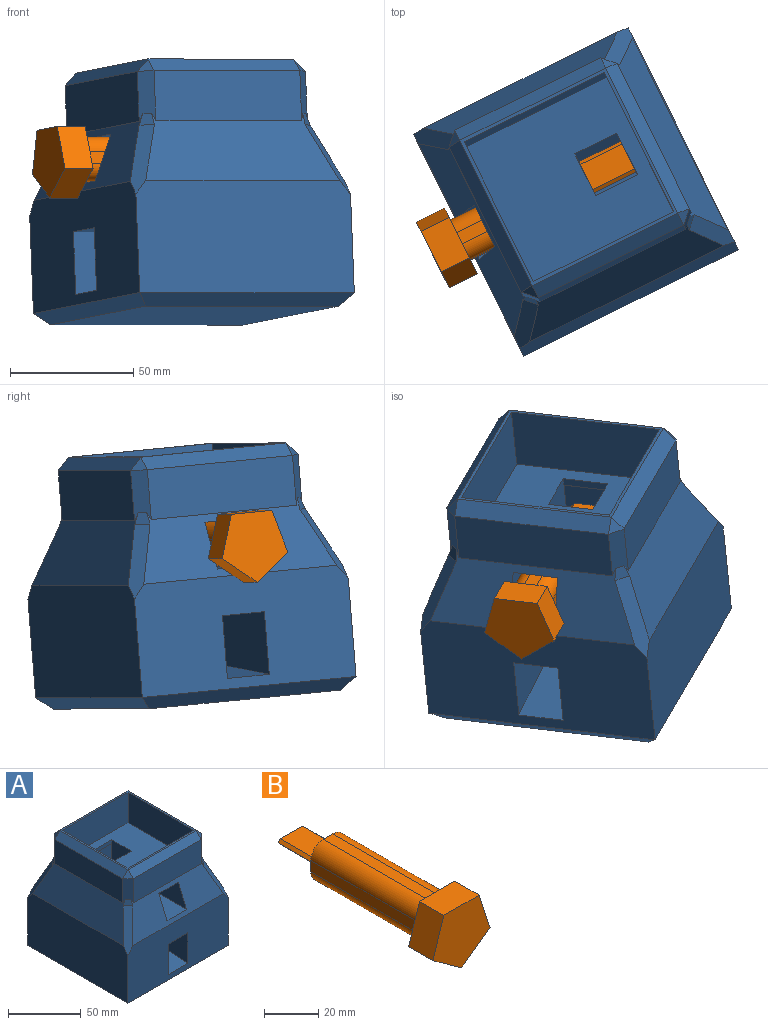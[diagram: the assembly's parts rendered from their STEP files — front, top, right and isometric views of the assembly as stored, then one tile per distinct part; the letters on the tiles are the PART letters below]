
ASSEMBLY  parts=2 mates=1
PART A: 57 faces, bbox 97.2x97.2x101.6 mm
  f0: plane 38.1x19.05mm, normal (0,-1,0), area 725.8mm2, adj f10,f11,f12,f54
  f1: plane 19.05x19.05mm, normal (0,1,0), area 362.9mm2, adj f2,f11,f12,f13
  f2: plane 53.66x19.05mm, normal (0,0,1), area 1022.1mm2, adj f1,f11,f12,f14
  f3: plane 45.77x19.05mm, normal (0,0,-1), area 871.8mm2, adj f4,f11,f12,f14
  f4: plane 19.05x3.18mm, normal (0,1,0), area 60.5mm2, adj f3,f5,f11,f12
  f5: plane 63.5x63.5mm, normal (0,0,1), area 3669.3mm2, adj f4,f6,f11,f12,f20,f21,f22,f27
  f6: plane 19.05x3.18mm, normal (0,-1,0), area 60.5mm2, adj f5,f11,f12,f55
  f7: plane 87.86x28.41mm, normal (0.92,0,0.38), area 2131.3mm2, adj f17,f24,f34,f36,f46,f48,f50,f53
  f8: plane 87.08x27.47mm, normal (0,0.92,0.38), area 2042.9mm2, adj f25,f45,f46,f47,f48,f49,f50,f51
  f9: plane 87.86x28.41mm, normal (-0.92,0,0.38), area 2131.3mm2, adj f15,f26,f33,f35,f45,f47,f51,f52
  f10: plane 74.02x19.05mm, normal (0,-0.09,1), area 1415.5mm2, adj f0,f11,f12,f18
  f11: plane 74.05x66.8mm, normal (1,0,0), area 3383.5mm2, adj f0,f1,f2,f3,f4,f5,f6,f10
  f12: plane 74.05x66.8mm, normal (-1,0,0), area 3383.5mm2, adj f0,f1,f2,f3,f4,f5,f6,f10
  f13: plane 54.97x19.05mm, normal (0,0,-1), area 1047.2mm2, adj f1,f11,f12,f18
  f14: plane 87.86x28.41mm, normal (0,-0.92,0.38), area 1738.5mm2, adj f2,f3,f11,f12,f18,f23,f33,f34
  f15: plane 97.24x45.72mm, normal (-1,0,0), area 4419.3mm2, adj f9,f16,f18,f32,f33,f47
  f16: plane 97.24x44.71mm, normal (0,1,0), area 4329.7mm2, adj f15,f17,f30,f47,f48,f49
  f17: plane 97.24x45.72mm, normal (1,0,0), area 4419.3mm2, adj f7,f16,f18,f29,f34,f48
  f18: plane 97.24x45.72mm, normal (0,-1,0), area 3933mm2, adj f10,f11,f12,f13,f14,f15,f17,f31
  f19: plane 87.08x87.08mm, normal (0,0,-1), area 7583.3mm2, adj f29,f30,f31,f32
  f20: plane 63.5x25.4mm, normal (-1,0,0), area 1612.9mm2, adj f5,f21,f27,f28
  f21: plane 63.5x25.4mm, normal (0,1,0), area 1612.9mm2, adj f5,f20,f22,f28
  f22: plane 63.5x25.4mm, normal (1,0,0), area 1612.9mm2, adj f5,f21,f27,f28
  f23: plane 66.04x20.32mm, normal (0,-1,0), area 1341.9mm2, adj f14,f35,f36,f37
  f24: plane 66.04x20.32mm, normal (1,0,0), area 1341.9mm2, adj f7,f36,f41,f46
  f25: plane 66.04x20.32mm, normal (0,1,0), area 1341.9mm2, adj f8,f42,f45,f46
  f26: plane 66.04x20.32mm, normal (-1,0,0), area 1341.9mm2, adj f9,f35,f40,f45
  f27: plane 63.5x25.4mm, normal (0,-1,0), area 1612.9mm2, adj f5,f20,f22,f28
  f28: plane 66.04x66.04mm, normal (0,0,1), area 329mm2, adj f20,f21,f22,f27,f37,f40,f41,f42
  f29: plane 97.24x5.08mm, normal (0.71,0,-0.71), area 662.1mm2, adj f17,f19,f30,f31
  f30: plane 97.24x5.08mm, normal (0,0.71,-0.71), area 662.1mm2, adj f16,f19,f29,f32
  f31: plane 97.24x5.08mm, normal (0,-0.71,-0.71), area 662.1mm2, adj f18,f19,f29,f32
  f32: plane 97.24x5.08mm, normal (-0.71,0,-0.71), area 662.1mm2, adj f15,f19,f30,f31
  f33: plane 29.34x14.5mm, normal (-0.61,-0.61,0.51), area 203.9mm2, adj f9,f14,f15,f18,f52
  f34: plane 29.34x14.5mm, normal (0.61,-0.61,0.51), area 203.9mm2, adj f7,f14,f17,f18,f53
  f35: plane 20.32x5.08mm, normal (-0.71,-0.71,0), area 129.7mm2, adj f9,f14,f23,f26,f38,f52
  f36: plane 20.32x5.08mm, normal (0.71,-0.71,0), area 129.7mm2, adj f7,f14,f23,f24,f39,f53
  f37: plane 66.04x5.08mm, normal (0,-0.71,0.71), area 474.4mm2, adj f23,f28,f38,f39
  f38: plane 5.08x5.08mm, normal (-0.58,-0.58,0.58), area 22.3mm2, adj f35,f37,f40
  f39: plane 5.08x5.08mm, normal (0.58,-0.58,0.58), area 22.3mm2, adj f36,f37,f41
  f40: plane 66.04x5.08mm, normal (-0.71,0,0.71), area 474.4mm2, adj f26,f28,f38,f43
  f41: plane 66.04x5.08mm, normal (0.71,0,0.71), area 474.4mm2, adj f24,f28,f39,f44
  f42: plane 66.04x5.08mm, normal (0,0.71,0.71), area 474.4mm2, adj f25,f28,f43,f44
  f43: plane 5.08x5.08mm, normal (-0.58,0.58,0.58), area 22.3mm2, adj f40,f42,f45
  f44: plane 5.08x5.08mm, normal (0.58,0.58,0.58), area 22.3mm2, adj f41,f42,f46
  f45: plane 20.32x5.08mm, normal (-0.71,0.71,0), area 129.7mm2, adj f8,f9,f25,f26,f43,f51
  f46: plane 20.32x5.08mm, normal (0.71,0.71,0), area 129.7mm2, adj f7,f8,f24,f25,f44,f50
  f47: plane 29.34x14.5mm, normal (-0.61,0.61,0.51), area 203.6mm2, adj f8,f9,f15,f16,f49,f51
  f48: plane 29.34x14.5mm, normal (0.61,0.61,0.51), area 203.6mm2, adj f7,f8,f16,f17,f49,f50
  f49: plane 89.53x1.94mm, normal (0,0.98,0.2), area 175mm2, adj f8,f16,f47,f48
  f50: plane 4.73x4.69mm, normal (0.68,0.68,0.26), area 25.2mm2, adj f7,f8,f46,f48
  f51: plane 4.73x4.69mm, normal (-0.68,0.68,0.26), area 25.2mm2, adj f8,f9,f45,f47
  f52: plane 4.73x4.69mm, normal (-0.68,-0.68,0.26), area 25.2mm2, adj f9,f14,f33,f35
  f53: plane 4.73x4.69mm, normal (0.68,-0.68,0.26), area 25.2mm2, adj f7,f14,f34,f36
  f54: plane 19.05x0.03mm, normal (0,0,1), area 0.5mm2, adj f0,f11,f12,f56
  f55: plane 19.05x0.03mm, normal (0,0,-1), area 0.5mm2, adj f6,f11,f12,f56
  f56: plane 19.05x19.05mm, normal (0,-1,0), area 362.9mm2, adj f11,f12,f54,f55
PART B: 23 faces, bbox 29.9x88.9x28.4 mm
  f0: plane 57.15x5.08mm, normal (1,0,0), area 290.3mm2, adj f4,f6,f10,f16
  f1: plane 57.15x5.08mm, normal (-1,0,0), area 290.3mm2, adj f5,f7,f10,f16
  f2: plane 57.15x5.08mm, normal (0,0,1), area 290.3mm2, adj f6,f7,f10,f16
  f3: plane 57.15x5.08mm, normal (0,0,-1), area 290.3mm2, adj f4,f5,f10,f16
  f4: cylinder r=6.35mm len=57.15mm, axis (0,1,0), area 570mm2, adj f0,f3,f10,f16
  f5: cylinder r=6.35mm len=57.15mm, axis (0,-1,0), area 570mm2, adj f1,f3,f10,f16
  f6: cylinder r=6.35mm len=57.15mm, axis (0,-1,0), area 570mm2, adj f0,f2,f10,f16
  f7: cylinder r=6.35mm len=57.15mm, axis (0,1,0), area 570mm2, adj f1,f2,f10,f16
  f8: plane 19.05x11.52mm, normal (0,0,1), area 219.5mm2, adj f10,f11,f13,f14
  f9: plane 19.05x11.52mm, normal (0,0,-1), area 219.5mm2, adj f10,f11,f12,f15
  f10: plane 17.78x17.78mm, normal (0,1,0), area 249mm2, adj f0,f1,f2,f3,f4,f5,f6,f7
  f11: plane 14.06x2.54mm, normal (0,1,0), area 32.5mm2, adj f8,f9,f12,f13,f14,f15
  f12: plane 19.05x1.27mm, normal (-0.71,0,-0.71), area 34.2mm2, adj f9,f10,f11,f13
  f13: plane 19.05x1.27mm, normal (-0.71,0,0.71), area 34.2mm2, adj f8,f10,f11,f12
  f14: plane 19.05x1.27mm, normal (0.71,0,0.71), area 34.2mm2, adj f8,f10,f11,f15
  f15: plane 19.05x1.27mm, normal (0.71,0,-0.71), area 34.2mm2, adj f9,f10,f11,f14
  f16: plane 29.86x28.4mm, normal (0,1,0), area 304.4mm2, adj f0,f1,f2,f3,f4,f5,f6,f7
  f17: plane 17.55x12.7mm, normal (0.95,0,0.31), area 234.4mm2, adj f16,f18,f21,f22
  f18: plane 18.45x12.7mm, normal (0,0,1), area 234.4mm2, adj f16,f17,f19,f22
  f19: plane 17.55x12.7mm, normal (-0.95,0,0.31), area 234.4mm2, adj f16,f18,f20,f22
  f20: plane 14.93x12.7mm, normal (-0.59,0,-0.81), area 234.4mm2, adj f16,f19,f21,f22
  f21: plane 14.93x12.7mm, normal (0.59,0,-0.81), area 234.4mm2, adj f16,f17,f20,f22
  f22: plane 29.86x28.4mm, normal (0,-1,0), area 585.9mm2, adj f17,f18,f19,f20,f21
PLACE A rot(axis=(-0.04,-0.07,-1),63.8deg) t=(-95.09,111.32,-78.16)mm
PLACE B rot(axis=(-0.04,-0.07,-1),63.8deg) t=(-82.43,-28.2,-11.83)mm
MATE slider A.f56 <-> B.f22  axis (-0.9,-0.44,0) through (-74.74,127.63,-14.92)mm
